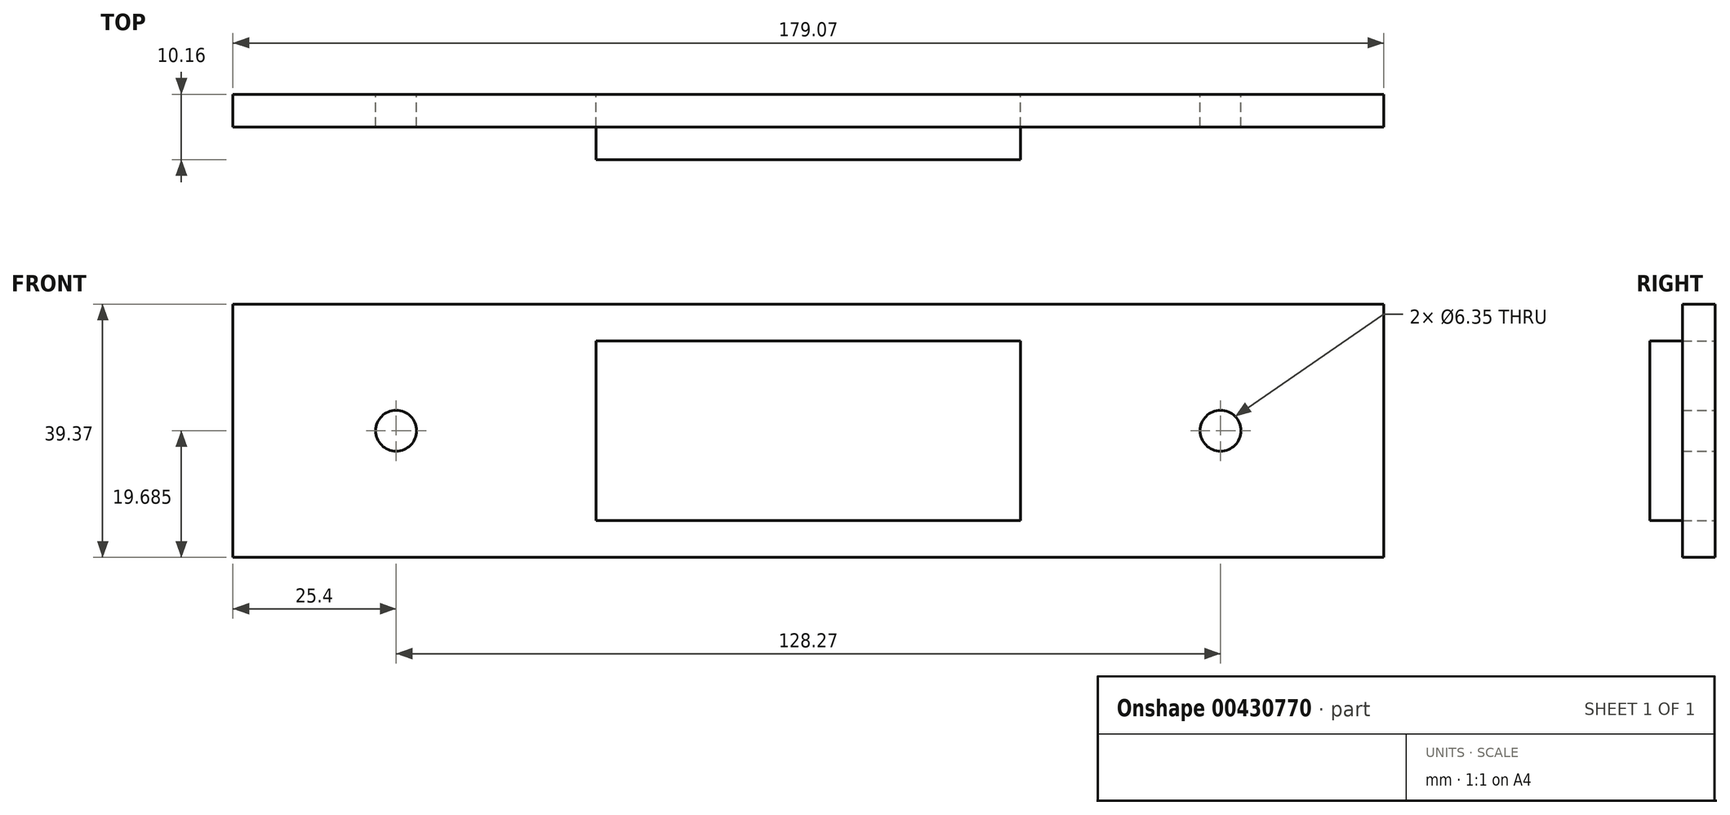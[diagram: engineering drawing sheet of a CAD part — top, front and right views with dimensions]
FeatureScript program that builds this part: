
annotation { "Feature Type Name" : "Feature", "Feature Type Description" : "" }
export const myFeature = defineFeature(function(context is Context, id is Id, definition is map)
    precondition{}
    {
        {
            var Q0;
            Q0=qCreatedBy(makeId("Front.planeOp"),FACE);
            var sketch = newSketch(context, id + "F0", { "sketchPlane" : qUnion([Q0])});
            skLineSegment(sketch, "E0.bottom", {"start": v(0, 0) * mm, "end": v(179.07, 0) * mm});
            skLineSegment(sketch, "E0.top", {"start": v(0, 39.37) * mm, "end": v(179.07, 39.37) * mm});
            skLineSegment(sketch, "E0.left", {"start": v(0, 0) * mm, "end": v(0, 39.37) * mm});
            skLineSegment(sketch, "E0.right", {"start": v(179.07, 0) * mm, "end": v(179.07, 39.37) * mm});
            skLineSegment(sketch, "E1.bottom", {"start": v(56.52, 33.66) * mm, "end": v(122.56, 33.66) * mm});
            skLineSegment(sketch, "E1.top", {"start": v(56.52, 5.71) * mm, "end": v(122.56, 5.71) * mm});
            skLineSegment(sketch, "E1.left", {"start": v(56.52, 33.66) * mm, "end": v(56.52, 5.71) * mm});
            skLineSegment(sketch, "E1.right", {"start": v(122.56, 33.66) * mm, "end": v(122.56, 5.71) * mm});
            skLineSegment(sketch, "E2", {"start": v(89.54, 33.66) * mm, "end": v(89.54, 5.71) * mm, "construction": true});
            skLineSegment(sketch, "E3", {"start": v(56.52, 19.69) * mm, "end": v(122.56, 19.69) * mm, "construction": true});
            skCircle(sketch, "E4", {"center": v(25.4, 19.69) * mm, "radius": 3.18 * mm});
            skPoint(sketch, "E4.centerSnap0", {"position": v(0, 19.69) * mm});
            skCircle(sketch, "E5", {"center": v(153.67, 19.69) * mm, "radius": 3.18 * mm});
            skLineSegment(sketch, "E6", {"start": v(0, 19.69) * mm, "end": v(50.8, 19.69) * mm, "construction": true});
            skLineSegment(sketch, "E7", {"start": v(179.07, 19.69) * mm, "end": v(128.27, 19.69) * mm, "construction": true});
            skSolve(sketch);
        }
        {
            var Q0;
            Q0 = qSketchRegion(id + "F0", true);
            var Q1;
            Q1=makeQuery(id+"F0.imprint","IMPRINT",FACE,{"disambiguationData":[TD([[makeQuery(id+"F0.imprint","IMPRINT",EDGE,{"derivedFrom":sQuery(id+"F0.wireOp",EDGE,"E1.bottom")}),-1.0]])]});
            extrude(context, id + "F1", {"entities" : qUnion([Q0, Q1]), "depth" : 5.08 * mm});
        }
        {
            var Q0;
            Q0=makeQuery(id+"F0.imprint","IMPRINT",FACE,{"disambiguationData":[TD([[makeQuery(id+"F0.imprint","IMPRINT",EDGE,{"derivedFrom":sQuery(id+"F0.wireOp",EDGE,"E1.bottom")}),-1.0]])]});
            extrude(context, id + "F2", {"entities" : qUnion([Q0]), "depth" : 10.16 * mm});
        }
    });
